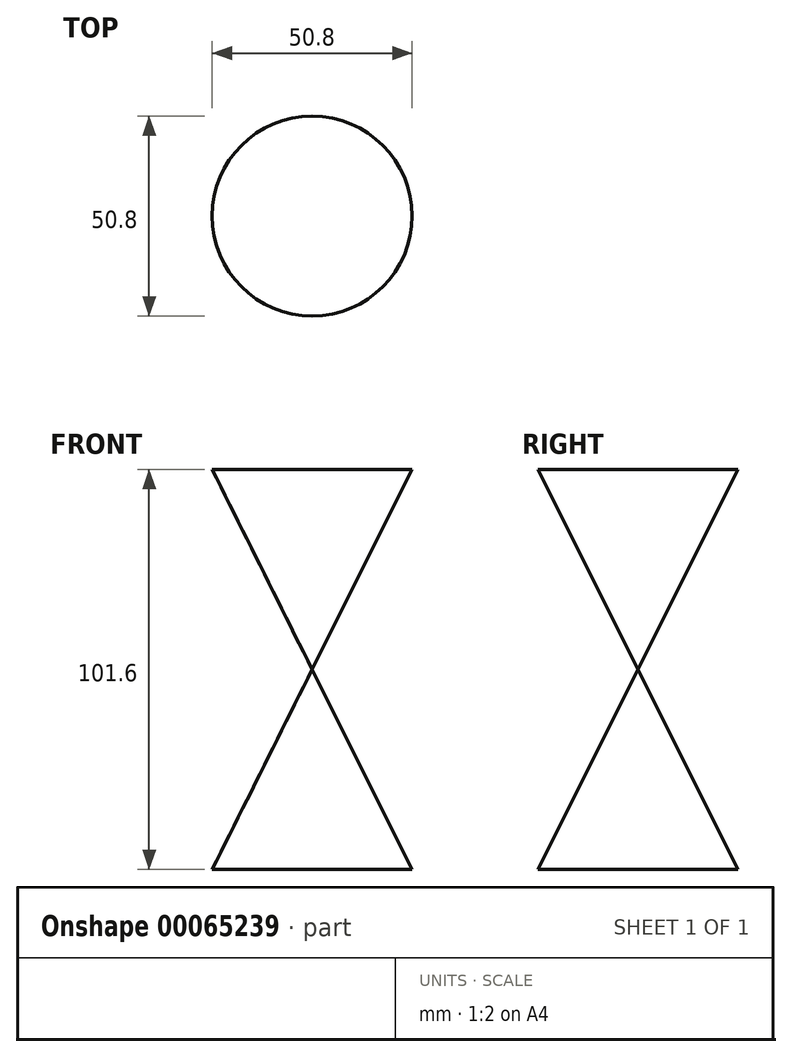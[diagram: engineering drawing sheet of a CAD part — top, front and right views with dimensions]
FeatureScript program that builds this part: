
annotation { "Feature Type Name" : "Feature", "Feature Type Description" : "" }
export const myFeature = defineFeature(function(context is Context, id is Id, definition is map)
    precondition{}
    {
        {
            var Q0;
            Q0=qCreatedBy(makeId("Front.planeOp"),FACE);
            var sketch = newSketch(context, id + "F0", { "sketchPlane" : qUnion([Q0])});
            skLineSegment(sketch, "E0", {"start": v(0, 0) * mm, "end": v(0, 50.8) * mm});
            skLineSegment(sketch, "E1", {"start": v(0, 50.8) * mm, "end": v(25.4, 0) * mm});
            skLineSegment(sketch, "E2", {"start": v(25.4, 0) * mm, "end": v(0, 0) * mm});
            skSolve(sketch);
        }
        {
            var Q0;
            Q0 = qSketchRegion(id + "F0", true);
            var Q1;
            Q1=sQuery(id+"F0.wireOp",EDGE,"E0");
            revolve(context, id + "F1", {"entities" : qUnion([Q0]), "axis" : qUnion([Q1]), "revolveType" : RevolveType.FULL});
        }
        {
            var Q0;
            Q0=qCreatedBy(makeId("Top.planeOp"),FACE);
            cPlane(context, id + "F2", {"entities" : qUnion([Q0]), "cplaneType" : CPlaneType.OFFSET, "offset" : 50.8 * mm, "width" : 152.4 * mm, "height" : 152.4 * mm});
        }
        {
            var Q0;
            Q0=makeQuery(id+"F1.opRevolve","SWEPT_BODY",BODY,{"disambiguationData":[OSD([sQuery(id+"F0.wireOp",EDGE,"E0"),sQuery(id+"F0.wireOp",EDGE,"E1"),sQuery(id+"F0.wireOp",EDGE,"E2")])]});
            var Q1;
            Q1=qCreatedBy(id+"F2.planeOp",FACE);
            mirror(context, id + "F3", {"entities" : qUnion([Q0]), "mirrorPlane" : qUnion([Q1])});
        }
        {
            var Q0;
            Q0=qCreatedBy(makeId("Front.planeOp"),FACE);
            cPlane(context, id + "F4", {"entities" : qUnion([Q0]), "cplaneType" : CPlaneType.OFFSET, "offset" : 12.7 * mm, "width" : 152.4 * mm, "height" : 152.4 * mm});
        }
        {
            var Q0;
            Q0=qCreatedBy(id+"F2.planeOp",FACE);
            cPlane(context, id + "F5", {"entities" : qUnion([Q0]), "cplaneType" : CPlaneType.OFFSET, "offset" : 25.4 * mm, "width" : 152.4 * mm, "height" : 152.4 * mm});
        }
        {
            var Q0;
            Q0=qCreatedBy(makeId("Front.planeOp"),FACE);
            var sketch = newSketch(context, id + "F6", { "sketchPlane" : qUnion([Q0])});
            skLineSegment(sketch, "E3", {"start": v(0, 50.8) * mm, "end": v(-25.4, 101.6) * mm});
            skLineSegment(sketch, "E4", {"start": v(25.4, 101.6) * mm, "end": v(0, 50.8) * mm});
            skLineSegment(sketch, "E5", {"start": v(0, 50.8) * mm, "end": v(25.4, 0) * mm});
            skLineSegment(sketch, "E6", {"start": v(-25.4, 0) * mm, "end": v(0, 50.8) * mm});
            skLineSegment(sketch, "E7", {"start": v(15.77, 82.35) * mm, "end": v(-37.4, 108.93) * mm, "construction": true});
            skLineSegment(sketch, "E8", {"start": v(-12.7, 76.2) * mm, "end": v(12.7, 76.2) * mm, "construction": true});
            skSolve(sketch);
        }
        {
            var Q0;
            Q0=sQuery(id+"F6.wireOp",EDGE,"E7");
            var Q1;
            Q1=sQuery(id+"F6.wireOp",VERTEX,"E7.start");
            cPlane(context, id + "F7", {"entities" : qUnion([Q0, Q1]), "cplaneType" : CPlaneType.LINE_POINT, "offset" : 152.4 * mm, "width" : 152.4 * mm, "height" : 152.4 * mm});
        }
        {
            var Q0;
            Q0=qCreatedBy(id+"F7.planeOp",FACE);
            cPlane(context, id + "F8", {"entities" : qUnion([Q0]), "cplaneType" : CPlaneType.OFFSET, "offset" : 25.4 * mm, "width" : 152.4 * mm, "height" : 152.4 * mm});
        }
        {
            var Q0;
            Q0=sQuery(id+"F6.wireOp",EDGE,"E8");
            var Q1;
            Q1=qCreatedBy(id+"F5.planeOp",FACE);
            cPlane(context, id + "F9", {"entities" : qUnion([Q0, Q1]), "cplaneType" : CPlaneType.LINE_ANGLE, "offset" : 152.4 * mm, "angle" : 15 * degree, "width" : 152.4 * mm, "height" : 152.4 * mm});
        }
    });
